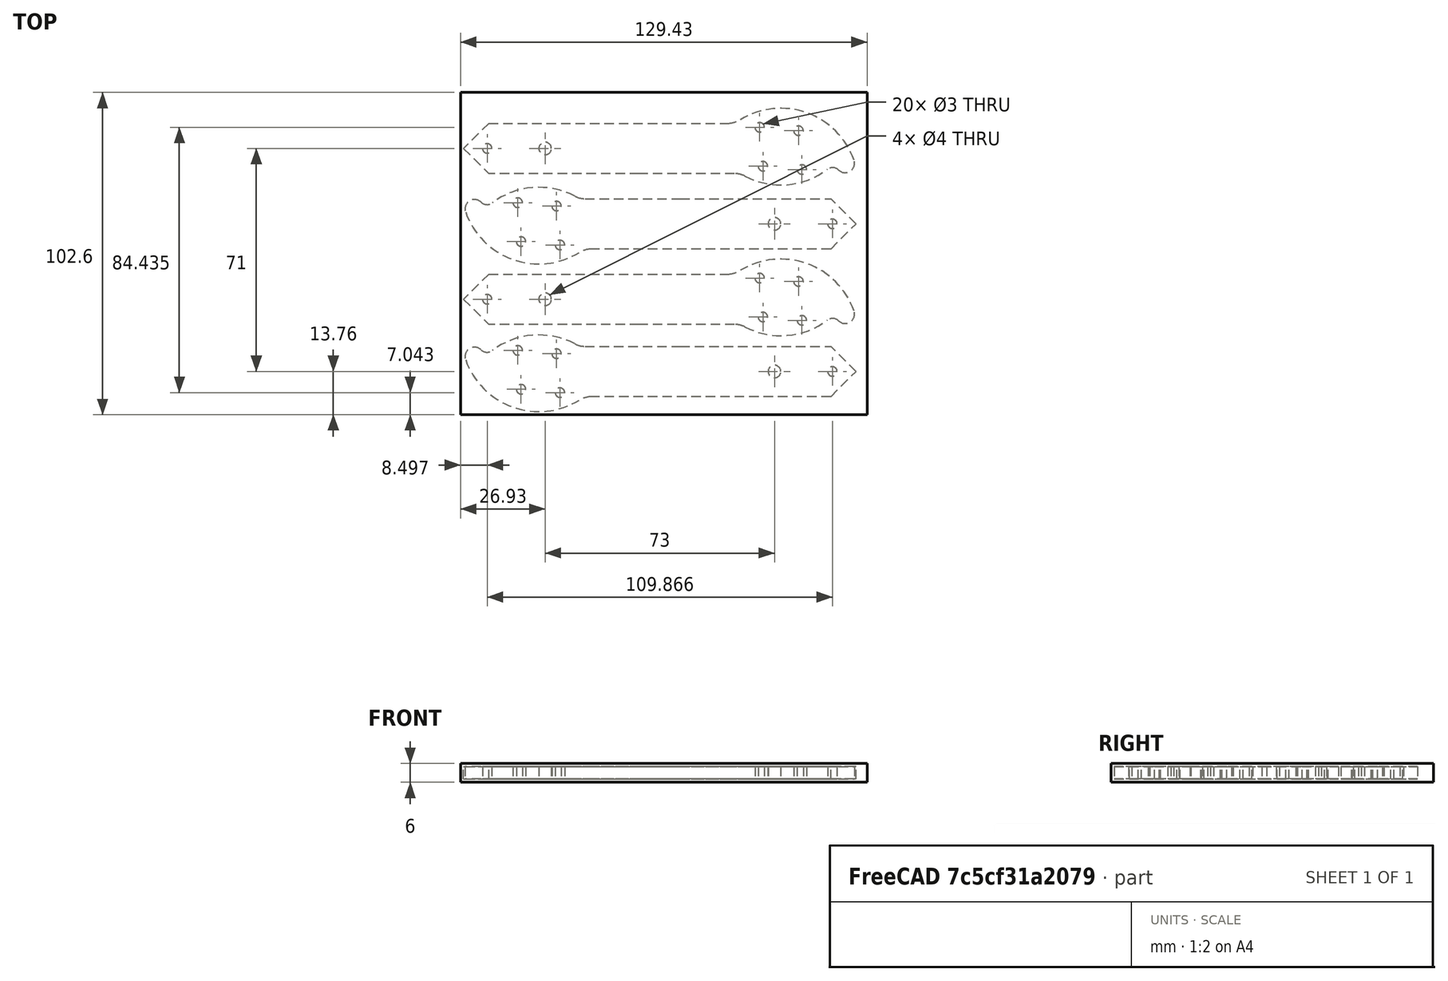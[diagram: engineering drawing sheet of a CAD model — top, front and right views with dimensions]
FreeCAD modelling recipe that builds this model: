
FCSTD DOCUMENT  (FreeCAD 0.18RUnknown)
Label: cam_arm
License: All rights reserved
LicenseURL: http://en.wikipedia.org/wiki/All_rights_reserved
objects: Path::FeaturePython×6, Part::FeaturePython×6, App::FeaturePython×1, Part::MultiFuse×1, App::DocumentObjectGroup×1, Path::FeatureCompoundPython×1
note: 8 computed .brp shape members not serialized (recipe doc carries the construction recipe); baked Part::Feature solids carry a one-line shape summary decoded from their .brp

FEATURE [App::FeaturePython] SetupSheet  # Path/CAM operation (typed FeaturePython)
  ClearanceHeightExpression = StartDepth+SetupSheet.ClearanceHeightOffset
  ClearanceHeightOffset = 5
  FinalDepthExpression = OpFinalDepth
  HorizRapid = 0
  SafeHeightExpression = StartDepth+SetupSheet.SafeHeightOffset
  SafeHeightOffset = 3
  StartDepthExpression = OpStartDepth
  StepDownExpression = OpToolDiameter
  VertRapid = 0
FEATURE [Path::FeaturePython] Default_Tool  label="Default Tool"  # Path/CAM operation (typed FeaturePython)
  HorizFeed = 10
  HorizRapid = 0
  SpindleDir = 0
  SpindleSpeed = 24000
  ToolNumber = 1
  VertFeed = 1.66667
  VertRapid = 0
  expr: Tool.Diameter = 3.175
  expr: VertFeed = 100mm / min
  expr: HorizFeed = 600mm / min
  expr: HorizRapid = SetupSheet.HorizRapid
  expr: VertRapid = SetupSheet.VertRapid
FEATURE [Path::FeaturePython] T2__drill  label="T2: drill"  # Path/CAM operation (typed FeaturePython)
  HorizFeed = 10
  HorizRapid = 0
  SpindleDir = 0
  SpindleSpeed = 12000
  ToolNumber = 2
  VertFeed = 1.66667
  VertRapid = 0
  expr: VertFeed = 100mm / min
  expr: HorizFeed = 600mm / min
  expr: HorizRapid = SetupSheet.HorizRapid
  expr: VertRapid = SetupSheet.VertRapid
FEATURE [Part::FeaturePython] arm_001  # a2plus imported part (geometry in sourceFile) (typed FeaturePython)
  Placement = pos=(25,15,0) rot=(0,0,1;1.5708rad)
  a2p_Version = V0.1
  fixedPosition = false
  sourceFile = ./arm.FCStd
  subassemblyImport = false
  timeLastImport = 1.55854e+09
  updateColors = true
FEATURE [Part::FeaturePython] arm_002  # a2plus imported part (geometry in sourceFile) (typed FeaturePython)
  Placement = pos=(102,38,0) rot=(0,0,-1;1.5708rad)
  a2p_Version = V0.1
  fixedPosition = true
  sourceFile = ./arm.FCStd
  subassemblyImport = false
  timeLastImport = 1.55854e+09
  updateColors = true
FEATURE [Part::FeaturePython] arm_003  # a2plus imported part (geometry in sourceFile) (typed FeaturePython)
  Placement = pos=(25,62,0) rot=(0,0,1;1.5708rad)
  a2p_Version = V0.1
  fixedPosition = false
  sourceFile = ./arm.FCStd
  subassemblyImport = false
  timeLastImport = 1.55854e+09
  updateColors = true
FEATURE [Part::FeaturePython] arm_004  # a2plus imported part (geometry in sourceFile) (typed FeaturePython)
  Placement = pos=(102,86,0) rot=(0,0,-1;1.5708rad)
  a2p_Version = V0.1
  fixedPosition = true
  sourceFile = ./arm.FCStd
  subassemblyImport = false
  timeLastImport = 1.55854e+09
  updateColors = true
FEATURE [Part::MultiFuse] Fusion
  Shapes = -> [arm_001,arm_002,arm_003,arm_004]
FEATURE [Part::FeaturePython] Clone  label="Base-arm_01"  # Draft clone (typed FeaturePython)
  AttacherType = Attacher::AttachEngine3D
  Fuse = false
  Objects = -> [Fusion]
  PathResource = Base
  Scale = (1,1,1)
FEATURE [App::DocumentObjectGroup] Model  label="Unnamed001"
  Group = -> [Clone]
FEATURE [Path::FeaturePython] Contour  # Path/CAM operation (typed FeaturePython)
  Active = true
  AreaParams:
    OpenMode = 0
    Angle = 45.0
    MinArcPoints = 4
    Coplanar = 2
    Tolerance = 1e-07
    CleanDistance = 0.0
    PocketExtraOffset = 0.0
    RoundPrecision = 0.0
    AngleShift = 0.0
    SubjectFill = 0
    PocketMode = 0
    PocketLastStepover = 0.0
    Simplify = False
    SectionTolerance = 1e-06
    MaxArcPoints = 100
    Offset = 1.5875
    Accuracy = 0.01
    LastStepover = 0.0
    PocketStepover = 0.0
    ClipFill = 0
    ToolRadius = 1.0
    Outline = False
    ClipperScale = 10000000.0
    FromCenter = False
    Explode = False
    EndType = 0
    Shift = 0.0
    ExtraPass = 0
    Project = False
    JoinType = 0
    Thicken = False
    Stepdown = 1.0
    SectionMode = 2
    MiterLimit = 2.0
    Deflection = 0.01
    Reorient = True
    FitArcs = True
    SectionCount = -1
    SectionOffset = 0.0
    Stepover = 0.0
    Unit = 1.0
    Fill = 0
  ClearanceHeight = 5
  Direction = 0
  FinalDepth = -3
  JoinType = 0
  MiterLimit = 0.1
  OffsetExtra = 0
  OpFinalDepth = -5
  OpStartDepth = 1
  OpStockZMax = 1
  OpStockZMin = -5
  OpToolDiameter = 3.175
  PathParams = {'resume_height': 3.0, 'feedrate': 10.0, 'verbose': True, 'orientation': 1, 'return_end': True, 'preamble': False, 'retraction': 5.0, 'feedrate_v': 1.6666666666666667}
  SafeHeight = 3
  Side = 0
  StartDepth = 0
  StartPoint = (0,0,0)
  StepDown = 0.5
  ToolController = -> Default_Tool
  UseComp = true
  UseStartPoint = false
  expr: ClearanceHeight = StartDepth + SetupSheet.ClearanceHeightOffset
  expr: SafeHeight = StartDepth + SetupSheet.SafeHeightOffset
  expr: StepDown = 0.5
  expr: FinalDepth = -3
  expr: StartDepth = 0
FEATURE [Part::FeaturePython] Stock001  # WARN: FeaturePython — macro-defined, semantics opaque (R4)
  Base = -> Model
  ExtXneg = 1
  ExtXpos = 1
  ExtYneg = 1
  ExtYpos = 1
  ExtZneg = 1
  ExtZpos = 1
  Placement = pos=(1.06676,2.23772,-4) rot=(0,0,1;0rad)
  StockType = FromBase
FEATURE [Path::FeaturePython] Drilling  # Path/CAM operation (typed FeaturePython)
  Active = true
  AddTipLength = false
  Base = -> [Clone]
  ClearanceHeight = 5
  DwellEnabled = false
  DwellTime = 0
  FinalDepth = -3
  OpFinalDepth = 0
  OpStartDepth = 1
  OpStockZMax = 1
  OpStockZMin = -5
  OpToolDiameter = 3
  PeckDepth = 0
  PeckEnabled = false
  RetractHeight = 10
  ReturnLevel = 0
  SafeHeight = 3
  StartDepth = 0
  ToolController = -> T2__drill
  expr: ClearanceHeight = StartDepth + SetupSheet.ClearanceHeightOffset
  expr: SafeHeight = StartDepth + SetupSheet.SafeHeightOffset
  expr: FinalDepth = -3
  expr: StartDepth = 0
FEATURE [Path::FeaturePython] TagDressup  # Path/CAM operation (typed FeaturePython)
  Angle = 45
  Base = -> Contour
  Disabled = [1,6,8,11,15,18,20]
  Height = 4
  Positions = (22) [(123.85,19.33,0),(122.97,9.79,0),(92.97,5.41,0),(38.12,4.15,0),(8.44,6.53,0),(60.53,24.59,0),(68.48,28.41,0),(3.97,32.86,0),(4.26,43.44,0),+13 more]
  Radius = 0
  SegmentationFactor = 50
  Width = 6
FEATURE [Path::FeatureCompoundPython] Operations001  label="Operations"  # Path/CAM operation (typed FeaturePython)
  Group = -> [Drilling,TagDressup]
  UsePlacements = false
FEATURE [Path::FeaturePython] Job  # Path/CAM operation (typed FeaturePython)
  GeometryTolerance = 0.01
  Model = -> Model
  Operations = -> Operations001
  PostProcessor = 6
  PostProcessorOutputFile = <userpath>/hs/fly/cad/gcode/arm
  SetupSheet = -> SetupSheet
  Stock = -> Stock001
  ToolController = -> [Default_Tool,T2__drill]
